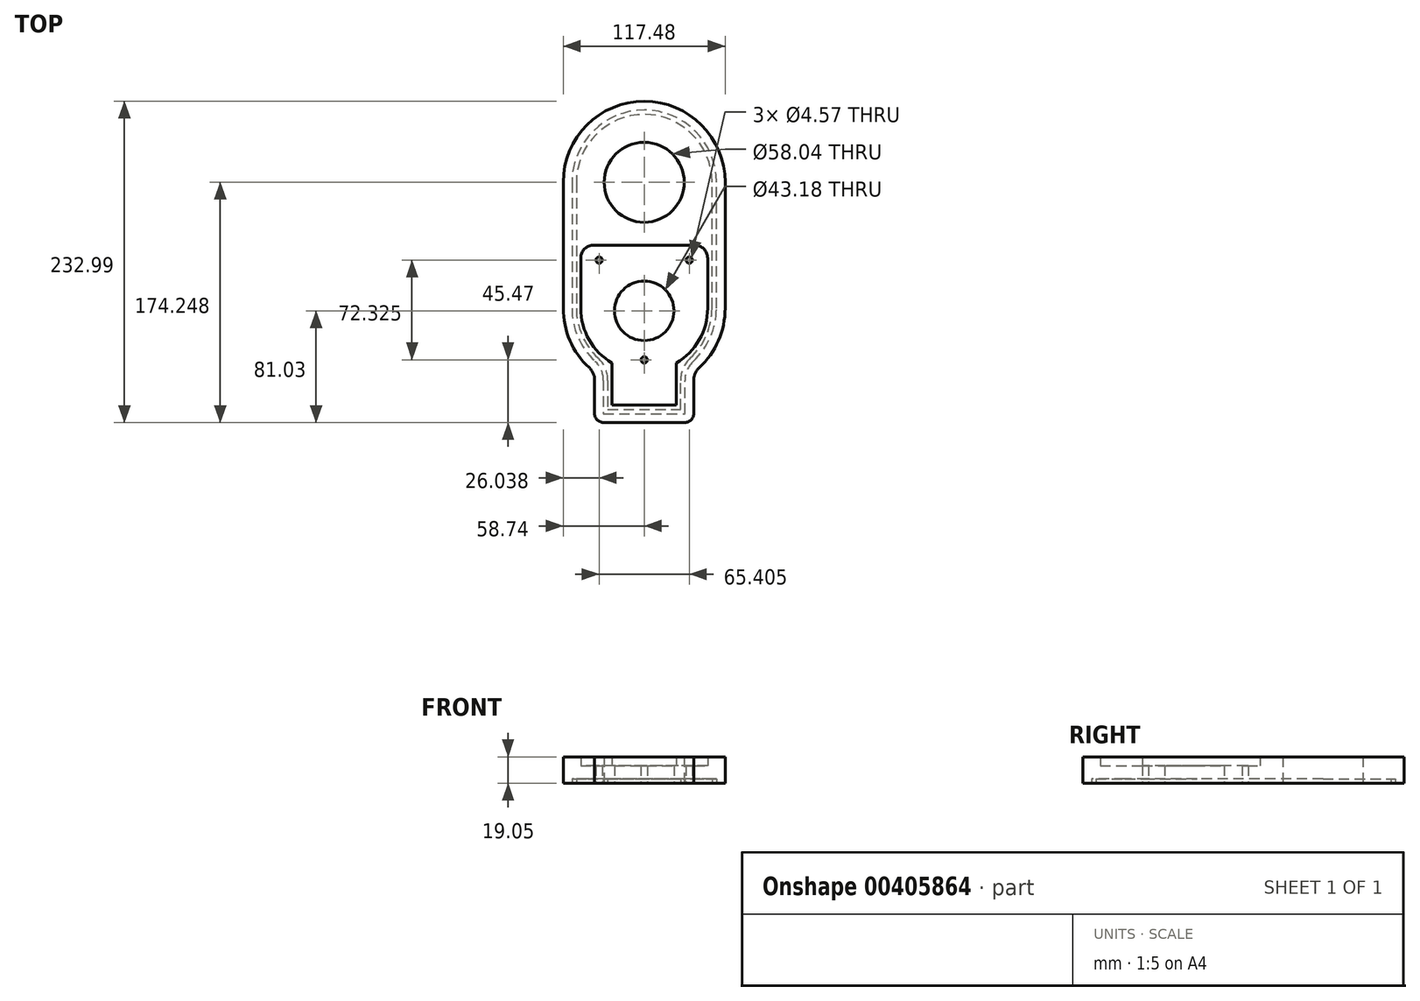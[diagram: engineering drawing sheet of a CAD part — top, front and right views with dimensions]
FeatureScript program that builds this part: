
annotation { "Feature Type Name" : "Feature", "Feature Type Description" : "" }
export const myFeature = defineFeature(function(context is Context, id is Id, definition is map)
    precondition{}
    {
        {
            var Q0;
            Q0=qCreatedBy(makeId("Top.planeOp"),FACE);
            var sketch = newSketch(context, id + "F0", { "sketchPlane" : qUnion([Q0]), "disableImprinting" : false});
            skCircle(sketch, "E0", {"center": v(-32.7, 36.77) * mm, "radius": 2.29 * mm});
            skCircle(sketch, "E1", {"center": v(32.7, 36.77) * mm, "radius": 2.29 * mm});
            skCircle(sketch, "E2", {"center": v(0, -35.56) * mm, "radius": 2.29 * mm});
            skCircle(sketch, "E3", {"center": v(0, 0) * mm, "radius": 21.59 * mm});
            skLineSegment(sketch, "E4", {"start": v(-32.7, 36.77) * mm, "end": v(32.7, 36.77) * mm, "construction": true});
            skLineSegment(sketch, "E5", {"start": v(0, -35.56) * mm, "end": v(32.7, 36.77) * mm, "construction": true});
            skLineSegment(sketch, "E6", {"start": v(0, -35.56) * mm, "end": v(-32.7, 36.77) * mm, "construction": true});
            skPoint(sketch, "E7", {"position": v(0, 21.59) * mm});
            skLineSegment(sketch, "E8", {"start": v(-46.04, 1.84) * mm, "end": v(-46.04, 38.16) * mm});
            skLineSegment(sketch, "E9", {"start": v(-36.51, 47.69) * mm, "end": v(36.51, 47.69) * mm});
            skLineSegment(sketch, "E10", {"start": v(46.04, 38.16) * mm, "end": v(46.04, 1.84) * mm});
            skPoint(sketch, "E11", {"position": v(0, 47.69) * mm});
            skLineSegment(sketch, "E12", {"start": v(-46.04, -44.2) * mm, "end": v(46.04, -44.2) * mm, "construction": true});
            skArc(sketch, "E13", {"start": v(-46.04, 1.84) * mm, "mid": v(-39.93, -21.07) * mm, "end": v(-23.24, -37.9) * mm});
            skCircle(sketch, "E14", {"center": v(0, 93.22) * mm, "radius": 29.02 * mm});
            skLineSegment(sketch, "E15", {"start": v(58.74, 93.22) * mm, "end": v(58.74, 1.84) * mm});
            skLineSegment(sketch, "E16", {"start": v(-58.74, 1.84) * mm, "end": v(-58.74, 93.22) * mm});
            skArc(sketch, "E17.trimOffspring", {"start": v(-58.74, 1.84) * mm, "mid": v(-53.85, -21.62) * mm, "end": v(-40, -41.18) * mm});
            skArc(sketch, "E18.trimOffspring", {"start": v(58.74, 93.22) * mm, "mid": v(0, 151.96) * mm, "end": v(-58.74, 93.22) * mm});
            skLineSegment(sketch, "E19", {"start": v(0, 0) * mm, "end": v(0, -88.44) * mm, "construction": true});
            skLineSegment(sketch, "E20.top", {"start": v(-29.6, -81.03) * mm, "end": v(29.6, -81.03) * mm});
            skLineSegment(sketch, "E20.left", {"start": v(-35.94, -50.48) * mm, "end": v(-35.94, -74.68) * mm});
            skLineSegment(sketch, "E20.right", {"start": v(35.94, -50.48) * mm, "end": v(35.94, -74.68) * mm});
            skArc(sketch, "E21.trimOffspring", {"start": v(40, -41.18) * mm, "mid": v(53.85, -21.62) * mm, "end": v(58.74, 1.84) * mm});
            skPoint(sketch, "E22.visualSharp", {"position": v(-35.94, -44.62) * mm});
            skArc(sketch, "E22.filletArc", {"start": v(-35.94, -50.48) * mm, "mid": v(-37, -45.4) * mm, "end": v(-40, -41.18) * mm});
            skPoint(sketch, "E23.visualSharp", {"position": v(35.94, -44.62) * mm});
            skArc(sketch, "E23.filletArc", {"start": v(40, -41.18) * mm, "mid": v(37, -45.4) * mm, "end": v(35.94, -50.48) * mm});
            skPoint(sketch, "E24.visualSharp", {"position": v(-35.94, -81.03) * mm});
            skArc(sketch, "E24.filletArc", {"start": v(-35.94, -74.68) * mm, "mid": v(-34.08, -79.17) * mm, "end": v(-29.6, -81.03) * mm});
            skPoint(sketch, "E25.visualSharp", {"position": v(35.94, -81.03) * mm});
            skArc(sketch, "E25.filletArc", {"start": v(29.6, -81.03) * mm, "mid": v(34.08, -79.17) * mm, "end": v(35.94, -74.68) * mm});
            skLineSegment(sketch, "E26.top", {"start": v(-23.24, -68.33) * mm, "end": v(23.24, -68.33) * mm});
            skLineSegment(sketch, "E26.left", {"start": v(-23.24, -37.9) * mm, "end": v(-23.24, -68.33) * mm});
            skLineSegment(sketch, "E26.right", {"start": v(23.24, -37.9) * mm, "end": v(23.24, -68.33) * mm});
            skArc(sketch, "E27.trimOffspring", {"start": v(23.24, -37.9) * mm, "mid": v(39.93, -21.07) * mm, "end": v(46.04, 1.84) * mm});
            skArc(sketch, "E28", {"start": v(-23.24, -37.9) * mm, "mid": v(0, -44.2) * mm, "end": v(23.24, -37.9) * mm, "construction": true});
            skPoint(sketch, "E29.visualSharp", {"position": v(-46.04, 47.69) * mm});
            skArc(sketch, "E29.filletArc", {"start": v(-36.51, 47.69) * mm, "mid": v(-43.25, 44.9) * mm, "end": v(-46.04, 38.16) * mm});
            skPoint(sketch, "E30.visualSharp", {"position": v(46.04, 47.69) * mm});
            skArc(sketch, "E30.filletArc", {"start": v(46.04, 38.16) * mm, "mid": v(43.25, 44.9) * mm, "end": v(36.51, 47.69) * mm});
            skSolve(sketch);
        }
        {
            var Q0;
            Q0=makeQuery(id+"F0.imprint","IMPRINT",FACE,{"disambiguationData":[TD([[makeQuery(id+"F0.imprint","IMPRINT",EDGE,{"derivedFrom":sQuery(id+"F0.wireOp",EDGE,"E8")}),1.0]])]});
            extrude(context, id + "F1", {"entities" : qUnion([Q0]), "depth" : 19.05 * mm});
        }
        {
            var Q0;
            Q0=makeQuery(id+"F1.opExtrude","CAP_FACE",FACE,{"disambiguationData":[OSD([sQuery(id+"F0.wireOp",EDGE,"E8"),sQuery(id+"F0.wireOp",EDGE,"E9"),sQuery(id+"F0.wireOp",EDGE,"E10"),sQuery(id+"F0.wireOp",EDGE,"E13"),sQuery(id+"F0.wireOp",EDGE,"E14"),sQuery(id+"F0.wireOp",EDGE,"E15"),sQuery(id+"F0.wireOp",EDGE,"E16"),sQuery(id+"F0.wireOp",EDGE,"E17.trimOffspring"),sQuery(id+"F0.wireOp",EDGE,"E18.trimOffspring"),sQuery(id+"F0.wireOp",EDGE,"E20.top"),sQuery(id+"F0.wireOp",EDGE,"E20.left"),sQuery(id+"F0.wireOp",EDGE,"E20.right"),sQuery(id+"F0.wireOp",EDGE,"E21.trimOffspring"),sQuery(id+"F0.wireOp",EDGE,"E22.filletArc"),sQuery(id+"F0.wireOp",EDGE,"E23.filletArc"),sQuery(id+"F0.wireOp",EDGE,"E24.filletArc"),sQuery(id+"F0.wireOp",EDGE,"E25.filletArc"),sQuery(id+"F0.wireOp",EDGE,"E26.top"),sQuery(id+"F0.wireOp",EDGE,"E26.left"),sQuery(id+"F0.wireOp",EDGE,"E26.right"),sQuery(id+"F0.wireOp",EDGE,"E27.trimOffspring"),sQuery(id+"F0.wireOp",EDGE,"E29.filletArc"),sQuery(id+"F0.wireOp",EDGE,"E30.filletArc")])],"isStart":true});
            var sketch = newSketch(context, id + "F2", { "sketchPlane" : qUnion([Q0])});
            skCircle(sketch, "E31.0", {"center": v(-32.7, -36.77) * mm, "radius": 2.29 * mm});
            skCircle(sketch, "E31.1", {"center": v(32.7, -36.77) * mm, "radius": 2.29 * mm});
            skCircle(sketch, "E31.2", {"center": v(0, 35.56) * mm, "radius": 2.29 * mm});
            skPoint(sketch, "E31.11", {"position": v(0, -47.69) * mm});
            skCircle(sketch, "E31.14", {"center": v(0, -93.22) * mm, "radius": 29.02 * mm});
            skLineSegment(sketch, "E31.15", {"start": v(58.74, -93.22) * mm, "end": v(58.74, -1.84) * mm});
            skLineSegment(sketch, "E31.16", {"start": v(-58.74, -1.84) * mm, "end": v(-58.74, -93.22) * mm});
            skArc(sketch, "E31.17", {"start": v(-58.74, -1.84) * mm, "mid": v(-53.85, 21.62) * mm, "end": v(-40, 41.18) * mm});
            skArc(sketch, "E31.18", {"start": v(58.74, -93.22) * mm, "mid": v(0, -151.96) * mm, "end": v(-58.74, -93.22) * mm});
            skLineSegment(sketch, "E31.20", {"start": v(-29.6, 81.03) * mm, "end": v(29.6, 81.03) * mm});
            skLineSegment(sketch, "E31.21", {"start": v(-35.94, 50.48) * mm, "end": v(-35.94, 74.68) * mm});
            skLineSegment(sketch, "E31.22", {"start": v(35.94, 50.48) * mm, "end": v(35.94, 74.68) * mm});
            skArc(sketch, "E31.23", {"start": v(40, 41.18) * mm, "mid": v(53.85, 21.62) * mm, "end": v(58.74, -1.84) * mm});
            skPoint(sketch, "E31.24", {"position": v(-35.94, 44.62) * mm});
            skArc(sketch, "E31.25", {"start": v(-35.94, 50.48) * mm, "mid": v(-37, 45.4) * mm, "end": v(-40, 41.18) * mm});
            skPoint(sketch, "E31.26", {"position": v(35.94, 44.62) * mm});
            skArc(sketch, "E31.27", {"start": v(40, 41.18) * mm, "mid": v(37, 45.4) * mm, "end": v(35.94, 50.48) * mm});
            skPoint(sketch, "E31.28", {"position": v(-35.94, 81.03) * mm});
            skArc(sketch, "E31.29", {"start": v(-35.94, 74.68) * mm, "mid": v(-34.08, 79.17) * mm, "end": v(-29.6, 81.03) * mm});
            skPoint(sketch, "E31.30", {"position": v(35.94, 81.03) * mm});
            skArc(sketch, "E31.31", {"start": v(29.6, 81.03) * mm, "mid": v(34.08, 79.17) * mm, "end": v(35.94, 74.68) * mm});
            skPoint(sketch, "E31.37", {"position": v(-46.04, -47.69) * mm});
            skCircle(sketch, "E32.0", {"center": v(0, 0) * mm, "radius": 21.59 * mm});
            skSolve(sketch);
        }
        {
            var Q0;
            Q0 = qSketchRegion(id + "F2", true);
            extrude(context, id + "F3", {"entities" : qUnion([Q0]), "operationType" : NewBodyOperationType.ADD, "oppositeDirection" : true, "depth" : 12.7 * mm});
        }
        {
            var Q0;
            Q0=makeQuery(id+"F0.imprint","IMPRINT",FACE,{"disambiguationData":[TD([[makeQuery(id+"F0.imprint","IMPRINT",EDGE,{"derivedFrom":sQuery(id+"F0.wireOp",EDGE,"E8")}),1.0]])]});
            var sketch = newSketch(context, id + "F4", { "sketchPlane" : qUnion([Q0])});
            skArc(sketch, "E33.0", {"start": v(-35.67, -36.53) * mm, "mid": v(-31.18, -42.87) * mm, "end": v(-29.6, -50.48) * mm});
            skArc(sketch, "E33.1", {"start": v(-52.39, 1.84) * mm, "mid": v(-48.03, -19.08) * mm, "end": v(-35.67, -36.53) * mm});
            skLineSegment(sketch, "E33.2", {"start": v(-29.6, -50.48) * mm, "end": v(-29.6, -74.68) * mm});
            skLineSegment(sketch, "E33.3", {"start": v(-52.39, 93.22) * mm, "end": v(-52.39, 1.84) * mm});
            skArc(sketch, "E33.4", {"start": v(52.39, 93.22) * mm, "mid": v(0, 145.6) * mm, "end": v(-52.39, 93.22) * mm});
            skLineSegment(sketch, "E33.5", {"start": v(52.39, 1.84) * mm, "end": v(52.39, 93.22) * mm});
            skLineSegment(sketch, "E33.6", {"start": v(-29.6, -74.68) * mm, "end": v(29.6, -74.68) * mm});
            skLineSegment(sketch, "E33.7", {"start": v(29.6, -74.68) * mm, "end": v(29.6, -50.48) * mm});
            skArc(sketch, "E33.8", {"start": v(29.6, -50.48) * mm, "mid": v(31.18, -42.87) * mm, "end": v(35.67, -36.53) * mm});
            skArc(sketch, "E33.9", {"start": v(35.67, -36.53) * mm, "mid": v(48.03, -19.08) * mm, "end": v(52.39, 1.84) * mm});
            skArc(sketch, "E34.0", {"start": v(-49.21, 1.84) * mm, "mid": v(-45.12, -17.82) * mm, "end": v(-33.5, -34.2) * mm});
            skLineSegment(sketch, "E34.1", {"start": v(-49.21, 93.22) * mm, "end": v(-49.21, 1.84) * mm});
            skArc(sketch, "E34.2", {"start": v(-33.5, -34.2) * mm, "mid": v(-28.27, -41.6) * mm, "end": v(-26.42, -50.48) * mm});
            skArc(sketch, "E34.3", {"start": v(49.21, 93.22) * mm, "mid": v(0, 142.43) * mm, "end": v(-49.21, 93.22) * mm});
            skLineSegment(sketch, "E34.4", {"start": v(49.21, 1.84) * mm, "end": v(49.21, 93.22) * mm});
            skArc(sketch, "E34.5", {"start": v(33.5, -34.2) * mm, "mid": v(45.12, -17.82) * mm, "end": v(49.21, 1.84) * mm});
            skLineSegment(sketch, "E34.6", {"start": v(-26.42, -50.48) * mm, "end": v(-26.42, -71.5) * mm});
            skLineSegment(sketch, "E34.7", {"start": v(-26.42, -71.5) * mm, "end": v(26.42, -71.5) * mm});
            skLineSegment(sketch, "E34.8", {"start": v(26.42, -71.5) * mm, "end": v(26.42, -50.48) * mm});
            skArc(sketch, "E34.9", {"start": v(26.42, -50.48) * mm, "mid": v(28.27, -41.6) * mm, "end": v(33.5, -34.2) * mm});
            skSolve(sketch);
        }
        {
            var Q0;
            Q0 = qSketchRegion(id + "F4", true);
            extrude(context, id + "F5", {"entities" : qUnion([Q0]), "operationType" : NewBodyOperationType.REMOVE, "depth" : 3.17 * mm, "offsetDistance" : 25.4 * mm});
        }
    });
